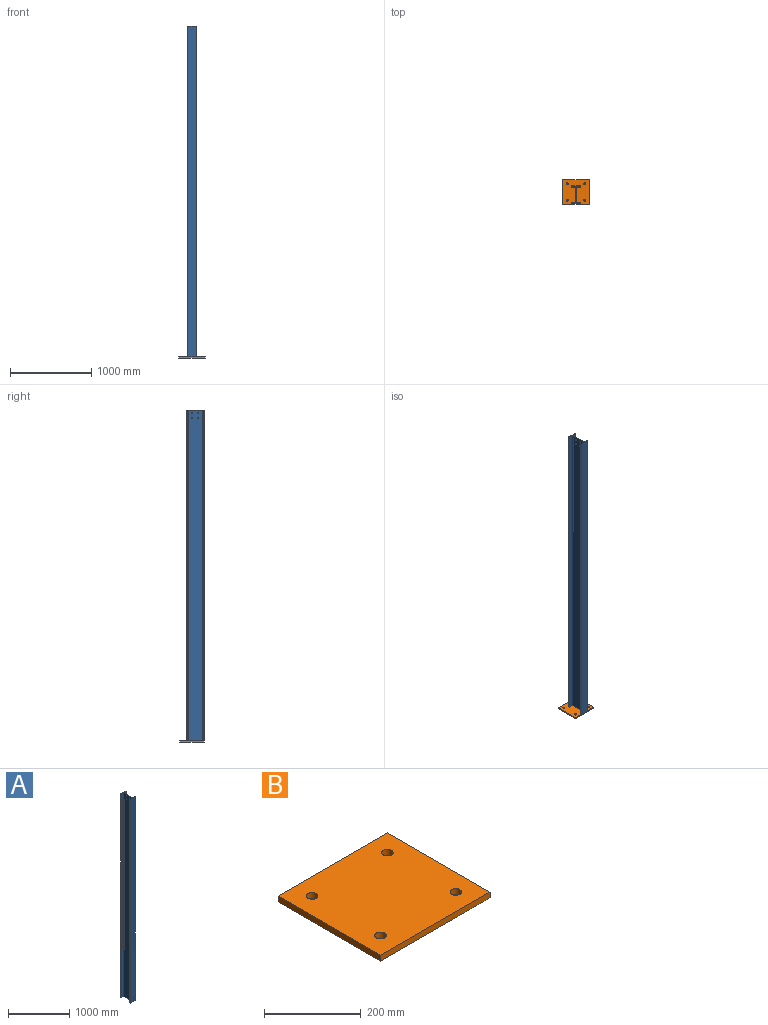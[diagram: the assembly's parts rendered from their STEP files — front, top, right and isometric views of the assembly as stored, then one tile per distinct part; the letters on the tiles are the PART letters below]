
ASSEMBLY  parts=2 mates=1
PART A: 22 faces, bbox 110x220x4069.6 mm
  f0: plane 220x110mm, normal (0,0,-1), area 3337.1mm2, adj f2,f3,f4,f5,f6,f7,f8,f9
  f1: plane 220x110mm, normal (0,0,1), area 3337.1mm2, adj f2,f3,f4,f5,f6,f7,f8,f9
  f2: plane 4069.6x40.05mm, normal (0,1,0), area 162987.5mm2, adj f0,f1,f3,f17
  f3: cylinder r=12mm len=4069.6mm, axis (0,0,1), area 76710.3mm2, adj f0,f1,f2,f4
  f4: plane 4069.6x177.6mm, normal (1,0,0), area 722145.2mm2, adj f0,f1,f3,f5,f18,f19,f20,f21
  f5: cylinder r=12mm len=4069.6mm, axis (0,0,1), area 76710.3mm2, adj f0,f1,f4,f6
  f6: plane 4069.6x40.05mm, normal (0,-1,0), area 162987.5mm2, adj f0,f1,f5,f7
  f7: plane 4069.6x9.2mm, normal (1,0,0), area 37440.3mm2, adj f0,f1,f6,f8
  f8: plane 4069.6x110mm, normal (0,1,0), area 447656mm2, adj f0,f1,f7,f9
  f9: plane 4069.6x9.2mm, normal (-1,0,0), area 37440.3mm2, adj f0,f1,f8,f10
  f10: plane 4069.6x40.05mm, normal (0,-1,0), area 162987.5mm2, adj f0,f1,f9,f11
  f11: cylinder r=12mm len=4069.6mm, axis (0,0,1), area 76710.3mm2, adj f0,f1,f10,f12
  f12: plane 4069.6x177.6mm, normal (-1,0,0), area 722145.2mm2, adj f0,f1,f11,f13,f18,f19,f20,f21
  f13: cylinder r=12mm len=4069.6mm, axis (0,0,1), area 76710.3mm2, adj f0,f1,f12,f14
  f14: plane 4069.6x40.05mm, normal (0,1,0), area 162987.5mm2, adj f0,f1,f13,f15
  f15: plane 4069.6x9.2mm, normal (-1,0,0), area 37440.3mm2, adj f0,f1,f14,f16
  f16: plane 4069.6x110mm, normal (0,-1,0), area 447656mm2, adj f0,f1,f15,f17
  f17: plane 4069.6x9.2mm, normal (1,0,0), area 37440.3mm2, adj f0,f1,f2,f16
  f18: cylinder r=7mm len=14mm, axis (1,0,0), area 259.5mm2, adj f4,f12
  f19: cylinder r=7mm len=14mm, axis (1,0,0), area 259.5mm2, adj f4,f12
  f20: cylinder r=7mm len=14mm, axis (1,0,0), area 259.5mm2, adj f4,f12
  f21: cylinder r=7mm len=14mm, axis (1,0,0), area 259.5mm2, adj f4,f12
PART B: 10 faces, bbox 320x300x15 mm
  f0: cylinder r=12mm len=24mm, axis (0,0,-1), area 1131mm2, adj f4,f5
  f1: cylinder r=12mm len=24mm, axis (0,0,-1), area 1131mm2, adj f4,f5
  f2: cylinder r=12mm len=24mm, axis (0,0,-1), area 1131mm2, adj f4,f5
  f3: cylinder r=12mm len=24mm, axis (0,0,-1), area 1131mm2, adj f4,f5
  f4: plane 320x300mm, normal (0,0,1), area 94190.4mm2, adj f0,f1,f2,f3,f6,f7,f8,f9
  f5: plane 320x300mm, normal (0,0,-1), area 94190.4mm2, adj f0,f1,f2,f3,f6,f7,f8,f9
  f6: plane 300x15mm, normal (-1,0,0), area 4500mm2, adj f4,f5,f7,f9
  f7: plane 320x15mm, normal (0,-1,0), area 4800mm2, adj f4,f5,f6,f8
  f8: plane 300x15mm, normal (1,0,0), area 4500mm2, adj f4,f5,f7,f9
  f9: plane 320x15mm, normal (0,1,0), area 4800mm2, adj f4,f5,f6,f8
PLACE A at identity
PLACE B t=(-160,-110,0)mm
MATE fastened B.f4 <-> A.f0  axis (0,0,1) through (0,-110,15)mm
